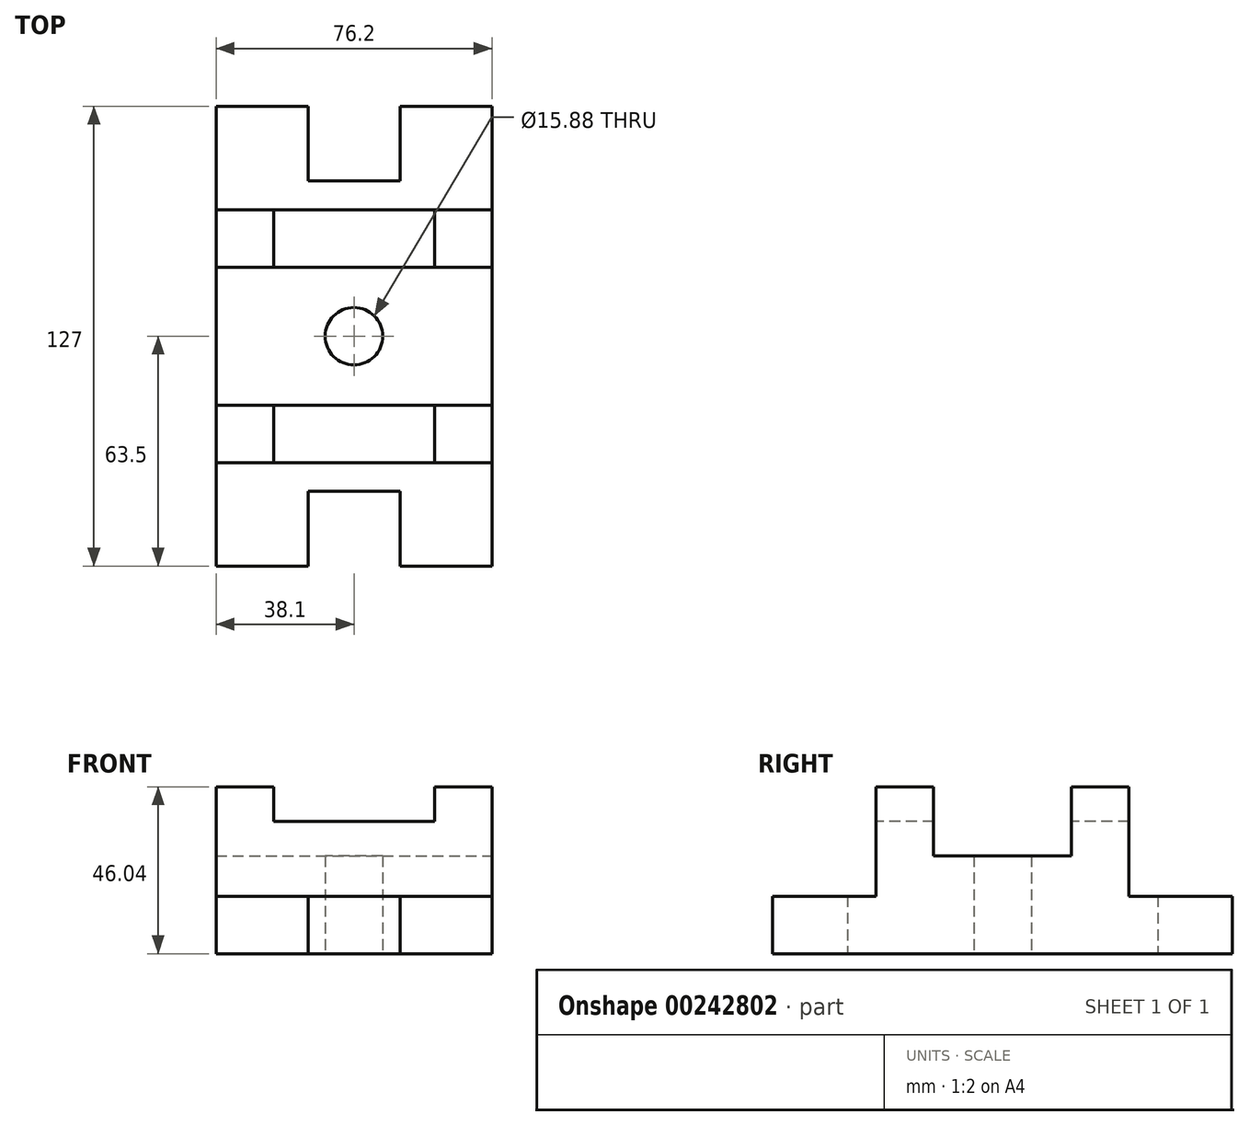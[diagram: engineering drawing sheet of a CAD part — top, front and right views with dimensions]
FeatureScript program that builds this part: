
annotation { "Feature Type Name" : "Feature", "Feature Type Description" : "" }
export const myFeature = defineFeature(function(context is Context, id is Id, definition is map)
    precondition{}
    {
        {
            var Q0;
            Q0=qCreatedBy(makeId("Top.planeOp"),FACE);
            var sketch = newSketch(context, id + "F0", { "sketchPlane" : qUnion([Q0])});
            skLineSegment(sketch, "E0", {"start": v(0, 15.88) * mm, "end": v(-25.4, 15.88) * mm});
            skLineSegment(sketch, "E1", {"start": v(-25.4, 15.88) * mm, "end": v(-25.4, 57.15) * mm});
            skLineSegment(sketch, "E2", {"start": v(-25.4, 57.15) * mm, "end": v(-76.2, 57.15) * mm});
            skLineSegment(sketch, "E3", {"start": v(-76.2, 57.15) * mm, "end": v(-76.2, 0) * mm});
            skLineSegment(sketch, "E4", {"start": v(-76.2, 0) * mm, "end": v(0, 0) * mm});
            skLineSegment(sketch, "E5", {"start": v(-76.2, 0) * mm, "end": v(-76.2, -31.75) * mm});
            skLineSegment(sketch, "E6.MirrorCS", {"start": v(25.4, 57.15) * mm, "end": v(76.2, 57.15) * mm});
            skLineSegment(sketch, "E7.MirrorCS", {"start": v(76.2, 57.15) * mm, "end": v(76.2, 0) * mm});
            skLineSegment(sketch, "E8.MirrorCS", {"start": v(25.4, 15.88) * mm, "end": v(25.4, 57.15) * mm});
            skLineSegment(sketch, "E9.MirrorCS", {"start": v(0, 15.88) * mm, "end": v(25.4, 15.88) * mm});
            skLineSegment(sketch, "E10.MirrorCS", {"start": v(76.2, 0) * mm, "end": v(76.2, -31.75) * mm});
            skPoint(sketch, "E11.MirrorCS.end.orphan", {"position": v(0, -31.22) * mm});
            skLineSegment(sketch, "E12", {"start": v(0, 0) * mm, "end": v(76.2, 0) * mm});
            skLineSegment(sketch, "E13", {"start": v(-76.2, -31.75) * mm, "end": v(76.2, -31.75) * mm});
            skLineSegment(sketch, "E14", {"start": v(-76.2, -31.75) * mm, "end": v(-76.2, -69.85) * mm});
            skLineSegment(sketch, "E15", {"start": v(76.2, -69.85) * mm, "end": v(76.2, -31.75) * mm});
            skLineSegment(sketch, "E16.MirrorCS", {"start": v(76.2, -31.75) * mm, "end": v(76.2, -69.85) * mm});
            skPoint(sketch, "E17.end.orphan", {"position": v(76.2, -50.8) * mm});
            skPoint(sketch, "E17.start.orphan", {"position": v(-76.2, -50.8) * mm});
            skLineSegment(sketch, "E18.MirrorCS", {"start": v(76.2, -69.85) * mm, "end": v(76.2, -107.95) * mm});
            skLineSegment(sketch, "E19.MirrorCS", {"start": v(-76.2, -107.95) * mm, "end": v(76.2, -107.95) * mm});
            skLineSegment(sketch, "E20.MirrorCS", {"start": v(-76.2, -139.7) * mm, "end": v(-76.2, -107.95) * mm});
            skLineSegment(sketch, "E21.MirrorCS", {"start": v(76.2, -139.7) * mm, "end": v(76.2, -107.95) * mm});
            skLineSegment(sketch, "E22.MirrorCS", {"start": v(0, -139.7) * mm, "end": v(76.2, -139.7) * mm});
            skLineSegment(sketch, "E23.MirrorCS", {"start": v(0, -155.57) * mm, "end": v(25.4, -155.57) * mm});
            skLineSegment(sketch, "E24.MirrorCS", {"start": v(0, -155.57) * mm, "end": v(-25.4, -155.57) * mm});
            skLineSegment(sketch, "E25.MirrorCS", {"start": v(-76.2, -139.7) * mm, "end": v(0, -139.7) * mm});
            skLineSegment(sketch, "E26.MirrorCS", {"start": v(-25.4, -155.58) * mm, "end": v(-25.4, -196.85) * mm});
            skLineSegment(sketch, "E27.MirrorCS", {"start": v(-25.4, -196.85) * mm, "end": v(-76.2, -196.85) * mm});
            skLineSegment(sketch, "E28.MirrorCS", {"start": v(-76.2, -196.85) * mm, "end": v(-76.2, -139.7) * mm});
            skLineSegment(sketch, "E29.MirrorCS", {"start": v(76.2, -196.85) * mm, "end": v(76.2, -139.7) * mm});
            skLineSegment(sketch, "E30.MirrorCS", {"start": v(25.4, -196.85) * mm, "end": v(76.2, -196.85) * mm});
            skLineSegment(sketch, "E31.MirrorCS", {"start": v(25.4, -155.58) * mm, "end": v(25.4, -196.85) * mm});
            skLineSegment(sketch, "E32", {"start": v(-44.45, 0) * mm, "end": v(-44.45, -31.75) * mm});
            skLineSegment(sketch, "E33", {"start": v(44.45, -31.75) * mm, "end": v(44.45, 0) * mm});
            skLineSegment(sketch, "E34", {"start": v(44.45, -107.95) * mm, "end": v(44.45, -139.7) * mm});
            skLineSegment(sketch, "E35", {"start": v(-44.45, -107.95) * mm, "end": v(-44.45, -139.7) * mm});
            skLineSegment(sketch, "E36", {"start": v(-76.2, -107.95) * mm, "end": v(-76.2, -69.85) * mm});
            skCircle(sketch, "E37", {"center": v(0, -69.85) * mm, "radius": 15.88 * mm});
            skSolve(sketch);
        }
        {
            var Q0;
            Q0=makeQuery(id+"F0.imprint","IMPRINT",FACE,{"disambiguationData":[TD([[makeQuery(id+"F0.imprint","IMPRINT",EDGE,{"derivedFrom":sQuery(id+"F0.wireOp",EDGE,"E0")}),1.0]])]});
            extrude(context, id + "F1", {"entities" : qUnion([Q0]), "depth" : 31.75 * mm});
        }
        {
            var Q0;
            {var subQ0=sQuery(id+"F0.wireOp",EDGE,"E5");Q0=makeQuery(id+"F0.imprint","IMPRINT",FACE,{"disambiguationData":[TD([[makeQuery(id+"F0.imprint","IMPRINT",EDGE,{"derivedFrom":subQ0}),1.0]])]});}
            extrude(context, id + "F2", {"entities" : qUnion([Q0]), "operationType" : NewBodyOperationType.ADD, "depth" : 92.07 * mm});
        }
        {
            var Q0;
            {var subQ0=sQuery(id+"F0.wireOp",EDGE,"E10.MirrorCS");Q0=makeQuery(id+"F0.imprint","IMPRINT",FACE,{"disambiguationData":[TD([[makeQuery(id+"F0.imprint","IMPRINT",EDGE,{"derivedFrom":subQ0}),-1.0]])]});}
            extrude(context, id + "F3", {"entities" : qUnion([Q0]), "operationType" : NewBodyOperationType.ADD, "depth" : 92.07 * mm});
        }
        {
            var Q0;
            {var subQ0=sQuery(id+"F0.wireOp",EDGE,"E20.MirrorCS");Q0=makeQuery(id+"F0.imprint","IMPRINT",FACE,{"disambiguationData":[TD([[makeQuery(id+"F0.imprint","IMPRINT",EDGE,{"derivedFrom":subQ0}),-1.0]])]});}
            extrude(context, id + "F4", {"entities" : qUnion([Q0]), "depth" : 92.07 * mm});
        }
        {
            var Q0;
            {var subQ0=sQuery(id+"F0.wireOp",EDGE,"E21.MirrorCS");Q0=makeQuery(id+"F0.imprint","IMPRINT",FACE,{"disambiguationData":[TD([[makeQuery(id+"F0.imprint","IMPRINT",EDGE,{"derivedFrom":subQ0}),1.0]])]});}
            extrude(context, id + "F5", {"entities" : qUnion([Q0]), "operationType" : NewBodyOperationType.ADD, "depth" : 92.07 * mm});
        }
        {
            var Q0;
            Q0=makeQuery(id+"F0.imprint","IMPRINT",FACE,{"disambiguationData":[TD([[makeQuery(id+"F0.imprint","IMPRINT",EDGE,{"derivedFrom":sQuery(id+"F0.wireOp",EDGE,"E23.MirrorCS")}),1.0]])]});
            extrude(context, id + "F6", {"entities" : qUnion([Q0]), "operationType" : NewBodyOperationType.ADD, "depth" : 31.75 * mm});
        }
        {
            var Q0;
            {var subQ4=sQuery(id+"F0.wireOp",EDGE,"E34");Q0=makeQuery(id+"F0.imprint","IMPRINT",FACE,{"disambiguationData":[TD([[makeQuery(id+"F0.imprint","IMPRINT",EDGE,{"derivedFrom":subQ4}),-1.0]])]});}
            extrude(context, id + "F7", {"entities" : qUnion([Q0]), "operationType" : NewBodyOperationType.ADD, "depth" : 73.02 * mm});
        }
        {
            var Q0;
            {var subQ0=sQuery(id+"F0.wireOp",EDGE,"E32");Q0=makeQuery(id+"F0.imprint","IMPRINT",FACE,{"disambiguationData":[TD([[makeQuery(id+"F0.imprint","IMPRINT",EDGE,{"derivedFrom":subQ0}),1.0]])]});}
            extrude(context, id + "F8", {"entities" : qUnion([Q0]), "operationType" : NewBodyOperationType.ADD, "depth" : 73.02 * mm});
        }
        {
            var Q0;
            {var subQ0=sQuery(id+"F0.wireOp",EDGE,"E14");Q0=makeQuery(id+"F0.imprint","IMPRINT",FACE,{"disambiguationData":[TD([[makeQuery(id+"F0.imprint","IMPRINT",EDGE,{"derivedFrom":subQ0}),1.0]])]});}
            extrude(context, id + "F9", {"entities" : qUnion([Q0]), "operationType" : NewBodyOperationType.ADD, "depth" : 53.97 * mm});
        }
        {
            var Q0;
            Q0=makeQuery(id+"F0.imprint","IMPRINT",FACE,{"disambiguationData":[TD([[makeQuery(id+"F0.imprint","IMPRINT",EDGE,{"derivedFrom":sQuery(id+"F0.wireOp",EDGE,"E37")}),1.0]])]});
            extrude(context, id + "F10", {"entities" : qUnion([Q0]), "operationType" : NewBodyOperationType.REMOVE, "oppositeDirection" : true, "depth" : 6.35 * mm});
        }
        {
            var Q0;
            Q0=makeQuery(id+"F9.opExtrude","SWEPT_BODY",BODY,{"disambiguationData":[OSD([sQuery(id+"F0.wireOp",EDGE,"E13"),sQuery(id+"F0.wireOp",EDGE,"E14"),sQuery(id+"F0.wireOp",EDGE,"E16.MirrorCS"),sQuery(id+"F0.wireOp",EDGE,"E18.MirrorCS"),sQuery(id+"F0.wireOp",EDGE,"E19.MirrorCS"),sQuery(id+"F0.wireOp",EDGE,"E36"),sQuery(id+"F0.wireOp",EDGE,"E37")])]});
            var Q1;
            Q1=makeQuery(id+"F7.opExtrude","SWEPT_BODY",BODY,{"disambiguationData":[OSD([sQuery(id+"F0.wireOp",EDGE,"E19.MirrorCS"),sQuery(id+"F0.wireOp",EDGE,"E22.MirrorCS"),sQuery(id+"F0.wireOp",EDGE,"E25.MirrorCS"),sQuery(id+"F0.wireOp",EDGE,"E34"),sQuery(id+"F0.wireOp",EDGE,"E35")])]});
            var Q2;
            Q2=makeQuery(id+"F5.opExtrude","SWEPT_BODY",BODY,{"disambiguationData":[OSD([sQuery(id+"F0.wireOp",EDGE,"E19.MirrorCS"),sQuery(id+"F0.wireOp",EDGE,"E21.MirrorCS"),sQuery(id+"F0.wireOp",EDGE,"E22.MirrorCS"),sQuery(id+"F0.wireOp",EDGE,"E34")])]});
            var Q3;
            Q3=makeQuery(id+"F4.opExtrude","SWEPT_BODY",BODY,{"disambiguationData":[OSD([sQuery(id+"F0.wireOp",EDGE,"E19.MirrorCS"),sQuery(id+"F0.wireOp",EDGE,"E20.MirrorCS"),sQuery(id+"F0.wireOp",EDGE,"E25.MirrorCS"),sQuery(id+"F0.wireOp",EDGE,"E35")])]});
            var Q4;
            Q4=makeQuery(id+"F1.opExtrude","SWEPT_BODY",BODY,{"disambiguationData":[OSD([sQuery(id+"F0.wireOp",EDGE,"E0"),sQuery(id+"F0.wireOp",EDGE,"E1"),sQuery(id+"F0.wireOp",EDGE,"E2"),sQuery(id+"F0.wireOp",EDGE,"E3"),sQuery(id+"F0.wireOp",EDGE,"E4"),sQuery(id+"F0.wireOp",EDGE,"E6.MirrorCS"),sQuery(id+"F0.wireOp",EDGE,"E7.MirrorCS"),sQuery(id+"F0.wireOp",EDGE,"E8.MirrorCS"),sQuery(id+"F0.wireOp",EDGE,"E9.MirrorCS"),sQuery(id+"F0.wireOp",EDGE,"E12")])]});
            var Q5;
            Q5=makeQuery(id+"F6.opExtrude","SWEPT_BODY",BODY,{"disambiguationData":[OSD([sQuery(id+"F0.wireOp",EDGE,"E22.MirrorCS"),sQuery(id+"F0.wireOp",EDGE,"E23.MirrorCS"),sQuery(id+"F0.wireOp",EDGE,"E24.MirrorCS"),sQuery(id+"F0.wireOp",EDGE,"E25.MirrorCS"),sQuery(id+"F0.wireOp",EDGE,"E26.MirrorCS"),sQuery(id+"F0.wireOp",EDGE,"E27.MirrorCS"),sQuery(id+"F0.wireOp",EDGE,"E28.MirrorCS"),sQuery(id+"F0.wireOp",EDGE,"E29.MirrorCS"),sQuery(id+"F0.wireOp",EDGE,"E30.MirrorCS"),sQuery(id+"F0.wireOp",EDGE,"E31.MirrorCS")])]});
            var Q6;
            Q6=makeQuery(id+"F6.opExtrude","CAP_VERTEX",VERTEX,{"disambiguationData":[OSD([sQuery(id+"F0.wireOp",EDGE,"E29.MirrorCS"),sQuery(id+"F0.wireOp",EDGE,"E30.MirrorCS")])],"isStart":true});
            transform(context, id + "F11", {"entities" : qUnion([Q0, Q1, Q2, Q3, Q4, Q5]), "transformType" : TransformType.SCALE_UNIFORMLY, "scale" : 1 / 2, "scalePoint" : qUnion([Q6]), "makeCopy" : false});
        }
    });
